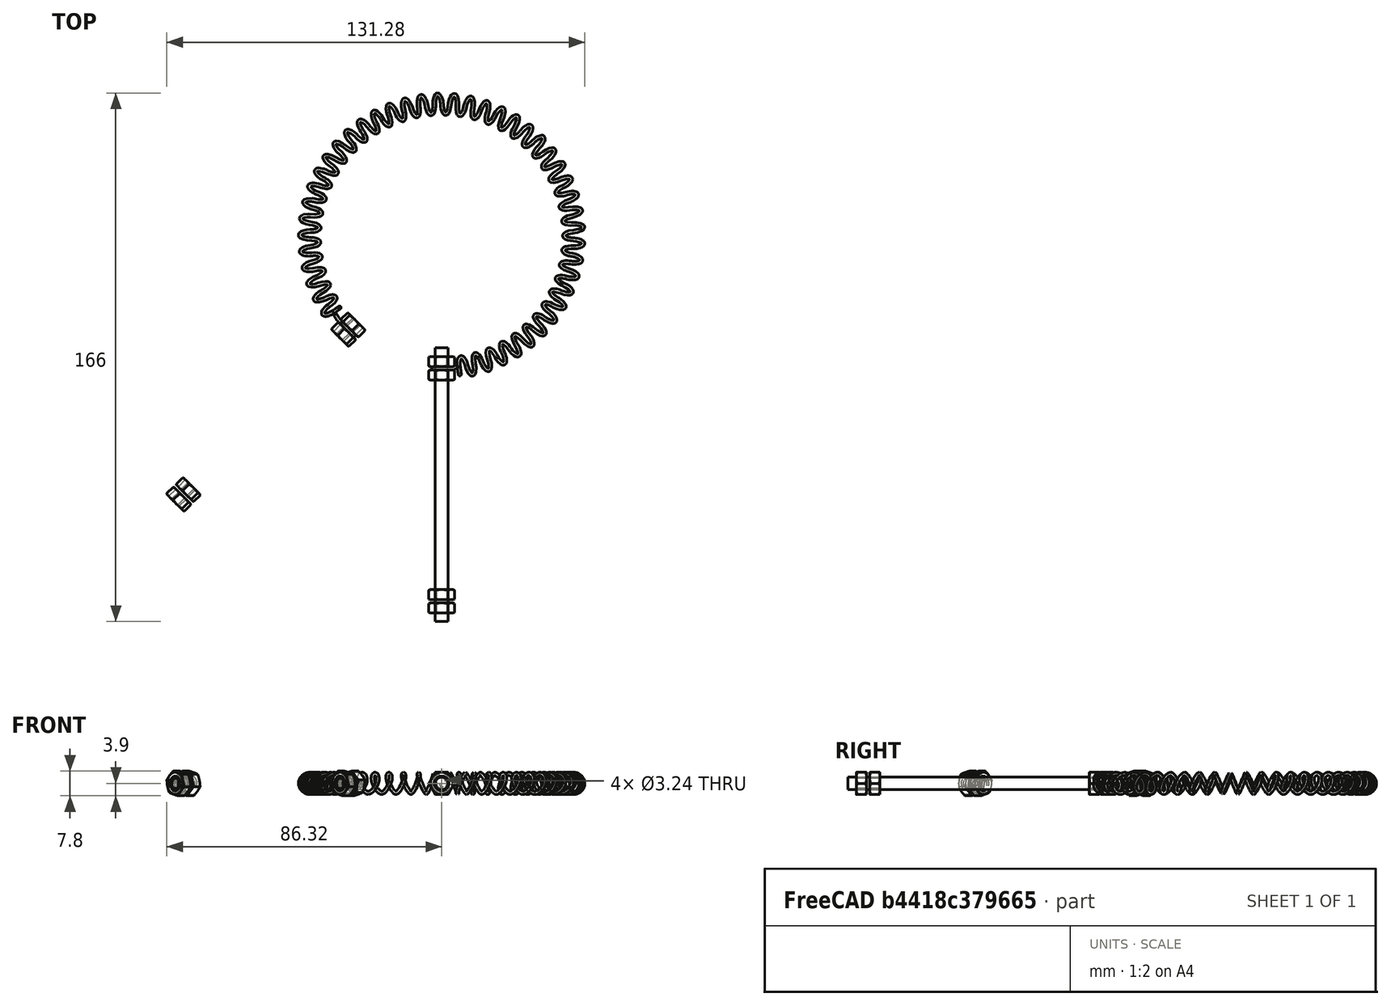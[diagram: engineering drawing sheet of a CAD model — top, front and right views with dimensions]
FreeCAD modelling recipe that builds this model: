
FCSTD DOCUMENT  (FreeCAD 1.0R39319 (Git))
Label: OCT-HELEM-A
License: Creative Commons Attribution 4.0
LicenseURL: https://creativecommons.org/licenses/by/4.0/
objects: Sketcher::SketchObject×9, Part::FeaturePython×9, PartDesign::Plane×3, PartDesign::SubShapeBinder×3, PartDesign::Line×2, PartDesign::Body×2, App::Part×2, App::LinkElement×2, App::VarSet×1, PartDesign::Point×1, PartDesign::AdditivePipe×1, PartDesign::Pad×1, App::Link×1, App::DocumentObjectGroup×1
note: 44 computed .brp shape members not serialized (recipe doc carries the construction recipe); baked Part::Feature solids carry a one-line shape summary decoded from their .brp

FEATURE [App::VarSet] VarSet  label="dims"
  arcAngle = 300
  barLength = 86
  brickThickness = 76
  chamberDiameter = 70
  coilDiameter = 6.02
  dTerminal = 4
  lWire = 866.98
  loopDiameter = 83
  pitch = 4.89634
  wireDiameter = 1.02
  expr: barLength = brickThickness + 10 mm
  expr: pitch = pi * coilDiameter * tan(asin(0.5 * loopDiameter * arcAngle * pi / (180 * lWire * 1 deg)))
FEATURE [Sketcher::SketchObject] Sketch006  label="coil path"
  ArcFitTolerance = 1e-06
  AttachmentSupport = -> [XY_Plane002]
  FullyConstrained = true
  MakeInternals = false
  MapMode = 5
  expr: Constraints[1] = <<dims>>.arcAngle
  expr: Constraints[3] = <<dims>>.loopDiameter / 2
  sketch-geometry (5):
    g0: ArcOfCircle CenterX=0 CenterY=0 CenterZ=0 NormalX=0 NormalY=0 NormalZ=1 AngleXU=0 Radius=41.5 StartAngle=4.84329 EndAngle=10.0793
    g1: LineSegment [constr] StartX=0 StartY=0 StartZ=0 EndX=-15.8814 EndY=-38.341 EndZ=0
    g2: LineSegment [constr] StartX=-32.9242 StartY=-25.2636 StartZ=0 EndX=-15.8814 EndY=-38.341 EndZ=0
    g3: LineSegment [constr] StartX=5.41684 StartY=-41.145 StartZ=0 EndX=-15.8814 EndY=-38.341 EndZ=0
    g4: LineSegment [constr] StartX=0 StartY=0 StartZ=0 EndX=-32.9242 EndY=-25.2636 EndZ=0
  constraints (14):
    c: Coincident(g0,g-1)
    c: Angle(g0) = 5.23599
    c: Coincident(g1,g0)
    c: Radius(g0) = 41.5
    c: PointOnObject(g1,g0)
    c: Coincident(g2,g0)
    c: Coincident(g2,g1)
    c: Coincident(g3,g0)
    c: Coincident(g3,g1)
    c: Equal(g2,g3)
    c: Coincident(g4,g0)
    c: Coincident(g4,g0)
    c: Angle(g-2,g4) = 2.22529
    c: Angle(g-2,g1) = 2.74889
FEATURE [PartDesign::Plane] DatumPlane  label="coil start right"
  AttachmentOffset = pos=(0,0,0) rot=(0,1,0;0.1309rad)
  AttachmentSupport = -> [YZ_Plane003]
  Length = 114.074
  MapMode = 5
  Placement = pos=(0,0,0) rot=(0.527011,0.600941,0.600941;2.17155rad)
  ResizeMode = 0
  Width = 64.1376
  expr: .AttachmentOffset.Rotation.Pitch = -22.5 + (360 - <<dims>>.arcAngle / deg) / 2
FEATURE [Part::FeaturePython] PathHelix  # WARN: FeaturePython — macro-defined, semantics opaque (R4)
  Count = 44.3787
  ExtraHalf = false
  Join = true
  Pitch = 4.89634
  Radius = 3.01
  Resolution = 4
  Reverse = true
  Rotation = 180
  Spine = -> Sketch006
  expr: Pitch = <<dims>>.pitch
  expr: Radius = <<dims>>.coilDiameter / 2
FEATURE [PartDesign::SubShapeBinder] Binder  label="loop binder"
  BindCopyOnChange = 0
  BindMode = 0
  ClaimChildren = false
  Context = -> Part [Part001.Body001.Binder.]
  Fuse = false
  MakeFace = true
  OffsetFill = false
  OffsetIntersection = false
  OffsetJoinType = 0
  OffsetOpenResult = false
  PartialLoad = false
  Relative = true
  Support = -> [Sketch006]
  _Version = 2
FEATURE [Sketcher::SketchObject] Sketch  label="terminal loop right"
  ArcFitTolerance = 1e-06
  AttachmentOffset = pos=(0,0,41.5) rot=(0,0,1;0rad)
  AttachmentSupport = -> [XZ_Plane003]
  FullyConstrained = true
  MakeInternals = false
  MapMode = 5
  Placement = pos=(0,-41.5,9.2e-15) rot=(1,0,0;1.5708rad)
  expr: .AttachmentOffset.Base.z = <<dims>>.loopDiameter / 2
  expr: Constraints[3] = (<<dims>>.dTerminal + <<dims>>.wireDiameter) / 2
  sketch-geometry (2):
    g0: ArcOfCircle CenterX=0 CenterY=0 CenterZ=0 NormalX=0 NormalY=0 NormalZ=1 AngleXU=0 Radius=2.51 StartAngle=0.288902 EndAngle=5.78669
    g1: ArcOfCircle CenterX=3.36454 CenterY=1 CenterZ=0 NormalX=0 NormalY=0 NormalZ=1 AngleXU=0 Radius=1 StartAngle=3.4305 EndAngle=4.71239
  constraints (6):
    c: Coincident(g0,g-1)
    c: Tangent(g0,g1) = 1.5708
    c: Tangent(g1,g-1) = -1.5708
    c: Radius(g0) = 2.51
    c: Radius(g1) = 1
    c: Angle(g0) = 5.49779
FEATURE [Sketcher::SketchObject] Sketch007  label="xy transition right"
  ArcFitTolerance = 1e-06
  AttachmentSupport = -> [XY_Plane003]
  ExternalGeometry = -> [Sketch,Binder]
  FullyConstrained = true
  MakeInternals = false
  MapMode = 5
  sketch-geometry (3):
    g0: ArcOfCircle CenterX=3.36454 CenterY=-40.4973 CenterZ=0 NormalX=0 NormalY=0 NormalZ=1 AngleXU=0 Radius=1.00271 StartAngle=4.71239 EndAngle=5.33537
    g1: ArcOfCircle CenterX=4.53463 CenterY=-42.126 CenterZ=0 NormalX=0 NormalY=0 NormalZ=1 AngleXU=0 Radius=1.00271 StartAngle=0.1309 EndAngle=2.19378
    g2: LineSegment [constr] StartX=5.52876 StartY=-41.9951 StartZ=0 EndX=0 EndY=0 EndZ=0
  constraints (7):
    c: Tangent(g1,g0) = 1.5708
    c: Tangent(g2,g1) = -1.5708
    c: Coincident(g2,g-1)
    c: PointOnObject(g-4,g2)
    c: PointOnObject(g0,g-4)
    c: Tangent(g-3,g0) = -1.5708
    c: Equal(g1,g0)
FEATURE [PartDesign::SubShapeBinder] Binder001  label="coil binder"
  BindCopyOnChange = 0
  BindMode = 0
  ClaimChildren = false
  Context = -> Part [Part001.Body001.Binder001.]
  Fuse = false
  MakeFace = true
  OffsetFill = false
  OffsetIntersection = false
  OffsetJoinType = 0
  OffsetOpenResult = false
  PartialLoad = false
  Relative = true
  Support = -> [PathHelix]
  _Version = 2
FEATURE [Sketcher::SketchObject] Sketch008  label="coil transition right"
  ArcFitTolerance = 1e-06
  AttachmentSupport = -> [DatumPlane]
  ExternalGeometry = -> [Binder001,Sketch007]
  FullyConstrained = true
  MakeInternals = false
  MapMode = 5
  Placement = pos=(0,0,0) rot=(0.527011,0.600941,0.600941;2.17155rad)
  expr: Constraints[1] = <<dims>>.loopDiameter / 2
  expr: Constraints[2] = <<dims>>.coilDiameter
  sketch-geometry (3):
    g0: Circle [constr] CenterX=-41.5 CenterY=0 CenterZ=0 NormalX=0 NormalY=0 NormalZ=1 AngleXU=0 Radius=3.01
    g1: ArcOfCircle CenterX=-42.3575 CenterY=1.38287 CenterZ=0 NormalX=0 NormalY=0 NormalZ=1 AngleXU=0 Radius=1.38287 StartAngle=2.12583 EndAngle=4.71238
    g2: ArcOfCircle CenterX=-41.5 CenterY=0 CenterZ=0 NormalX=0 NormalY=0 NormalZ=1 AngleXU=0 Radius=3.01 StartAngle=1.5708 EndAngle=2.12583
  constraints (8):
    c: PointOnObject(g0,g-1)
    c: DistanceX(g0,g-1) = 41.5
    c: Diameter(g0) = 6.02
    c: Coincident(g1,g-4)
    c: Tangent(g1,g-1)
    c: Coincident(g2,g-3)
    c: Coincident(g2,g0)
    c: Tangent(g1,g2) = -1.5708
FEATURE [Sketcher::SketchObject] Sketch009  label="wire cross section"
  ArcFitTolerance = 1e-06
  AttachmentSupport = -> [YZ_Plane003]
  FullyConstrained = true
  MakeInternals = false
  MapMode = 5
  Placement = pos=(0,0,0) rot=(0.57735,0.57735,0.57735;2.0944rad)
  expr: Constraints[0] = <<dims>>.wireDiameter
  expr: Constraints[1] = <<dims>>.loopDiameter / 2
  expr: Constraints[2] = (<<dims>>.dTerminal + <<dims>>.wireDiameter) / 2
  sketch-geometry (1):
    g0: Circle CenterX=-41.5 CenterY=-2.51 CenterZ=0 NormalX=0 NormalY=0 NormalZ=1 AngleXU=0 Radius=0.51
  constraints (3):
    c: Diameter(g0) = 1.02
    c: DistanceX(g0,g-1) = 41.5
    c: DistanceY(g0,g-1) = 2.51
FEATURE [PartDesign::Line] DatumLine  label="terminal axis left"
  AttacherType = Attacher::AttachEngineLine
  AttachmentOffset = pos=(0,0,0) rot=(0,-1,0;0.785398rad)
  AttachmentSupport = -> [Y_Axis003]
  Length = 20
  MapMode = 29
  Placement = pos=(0,0,0) rot=(0.281085,0.678598,0.678598;2.59356rad)
  ResizeMode = 0
FEATURE [PartDesign::Plane] DatumPlane001  label="terminal left plane"
  AttachmentOffset = pos=(0,0,41.5) rot=(0,0,1;0rad)
  AttachmentSupport = -> [DatumLine]
  Length = 142.427
  MapMode = 7
  Placement = pos=(-29.3449,-29.3449,0) rot=(0.862856,-0.357407,-0.357407;1.71777rad)
  ResizeMode = 0
  Width = 65.9072
  expr: .AttachmentOffset.Base.z = <<dims>>.loopDiameter / 2
FEATURE [Sketcher::SketchObject] Sketch010  label="terminal loop left"
  ArcFitTolerance = 1e-06
  AttachmentSupport = -> [DatumPlane001]
  FullyConstrained = true
  MakeInternals = false
  MapMode = 5
  Placement = pos=(-29.3449,-29.3449,0) rot=(0.862856,-0.357407,-0.357407;1.71777rad)
  expr: Constraints[1] = (<<dims>>.dTerminal + <<dims>>.wireDiameter) / 2
  sketch-geometry (2):
    g0: ArcOfCircle CenterX=0 CenterY=0 CenterZ=0 NormalX=0 NormalY=0 NormalZ=1 AngleXU=0 Radius=2.51 StartAngle=3.63809 EndAngle=9.13588
    g1: ArcOfCircle CenterX=-3.36454 CenterY=1 CenterZ=0 NormalX=0 NormalY=0 NormalZ=1 AngleXU=0 Radius=1 StartAngle=4.71239 EndAngle=5.99428
  constraints (6):
    c: Coincident(g0,g-1)
    c: Radius(g0) = 2.51
    c: Radius(g1) = 1
    c: Tangent(g1,g0) = 1.5708
    c: Tangent(g1,g-1) = -1.5708
    c: Angle(g0) = 5.49779
FEATURE [PartDesign::Point] DatumPoint  label="coil start point left"
  AttacherType = Attacher::AttachEnginePoint
  AttachmentSupport = -> [Binder001]
  MapMode = 37
  Placement = pos=(-34.0198,-23.7677,3.01) rot=(0,0,1;0rad)
FEATURE [PartDesign::Plane] DatumPlane002  label="coil start plane left"
  AttachmentSupport = -> [Binder001,Z_Axis003]
  Length = 140.493
  MapMode = 13
  Placement = pos=(-11.3399,-7.92258,1.33667) rot=(0.913595,0.287528,0.287528;1.66104rad)
  ResizeMode = 0
  Width = 65.7925
FEATURE [Sketcher::SketchObject] Sketch011  label="xy transition left"
  ArcFitTolerance = 1e-06
  AttachmentSupport = -> [XY_Plane003]
  ExternalGeometry = -> [Sketch010,Binder001]
  FullyConstrained = true
  MakeInternals = false
  MapMode = 5
  expr: Constraints[4] = <<dims>>.loopDiameter / 2
  sketch-geometry (4):
    g0: ArcOfCircle CenterX=-24.9661 CenterY=-20.2079 CenterZ=0 NormalX=0 NormalY=0 NormalZ=1 AngleXU=0 Radius=9.55715 StartAngle=3.60279 EndAngle=3.92699
    g1: ArcOfCircle CenterX=-32.6292 CenterY=-24.0161 CenterZ=0 NormalX=0 NormalY=0 NormalZ=1 AngleXU=0 Radius=1 StartAngle=2.18061 EndAngle=3.60279
    g2: LineSegment [constr] StartX=-33.5247 StartY=-24.4611 StartZ=0 EndX=0 EndY=3.6e-15 EndZ=0
    g3: LineSegment [constr] StartX=-34.0198 StartY=-23.7677 StartZ=0 EndX=0 EndY=0 EndZ=0
  constraints (9):
    c: Tangent(g0,g-3) = -1.5708
    c: Tangent(g0,g1) = -1.5708
    c: Coincident(g2,g0)
    c: Coincident(g2,g-1)
    c: Distance(g2,g2) = 41.5
    c: Coincident(g3,g-4)
    c: Coincident(g3,g2)
    c: Tangent(g1,g3) = 1.5708
    c: Radius(g1) = 1
FEATURE [Sketcher::SketchObject] Sketch012  label="coil transition left"
  ArcFitTolerance = 1e-06
  AttachmentSupport = -> [DatumPlane002]
  ExternalGeometry = -> [Sketch011,DatumPoint]
  FullyConstrained = true
  MakeInternals = false
  MapMode = 5
  Placement = pos=(-11.3399,-7.92258,1.33667) rot=(0.913595,0.287528,0.287528;1.66104rad)
  sketch-geometry (3):
    g0: Circle [constr] CenterX=-27.6579 CenterY=-1.33667 CenterZ=0 NormalX=0 NormalY=0 NormalZ=1 AngleXU=0 Radius=3.01001
    g1: ArcOfCircle CenterX=-26.6689 CenterY=0.00586924 CenterZ=0 NormalX=0 NormalY=0 NormalZ=1 AngleXU=0 Radius=1.34254 StartAngle=4.71239 EndAngle=7.21908
    g2: ArcOfCircle CenterX=-27.6579 CenterY=-1.33667 CenterZ=0 NormalX=0 NormalY=0 NormalZ=1 AngleXU=0 Radius=3.01001 StartAngle=0.935895 EndAngle=1.5737
  constraints (6):
    c: Coincident(g0,g-3)
    c: PointOnObject(g1,g0)
    c: Coincident(g2,g0)
    c: Tangent(g2,g1) = -1.5708
    c: Tangent(g1,g-3) = 1.5708
    c: Coincident(g2,g-4)
FEATURE [PartDesign::SubShapeBinder] Binder002  label="full path binder"
  BindCopyOnChange = 0
  BindMode = 0
  ClaimChildren = false
  Context = -> Part [Part001.Body001.Binder002.]
  Fuse = false
  MakeFace = true
  OffsetFill = false
  OffsetIntersection = false
  OffsetJoinType = 0
  OffsetOpenResult = false
  PartialLoad = false
  Refine = true
  Relative = true
  Support = -> [Sketch007,Sketch,Sketch011,Sketch008,Sketch010,Sketch012,Binder001]
  _Version = 2
FEATURE [PartDesign::AdditivePipe] AdditivePipe
  AuxilleryCurvelinear = true
  AuxillerySpineTangent = false
  Binormal = (0,0,0)
  Mode = 0
  Placement = pos=(0,0,0) rot=(1,1,1;2.0944rad)
  Profile = -> Sketch009
  Refine = true
  Spine = -> Binder002
  SpineTangent = false
  Suppressed = false
  Transformation = 0
  Transition = 0
FEATURE [PartDesign::Line] DatumLine001  label="terminal axis right"
  AttacherType = Attacher::AttachEngineLine
  AttachmentSupport = -> [Y_Axis003]
  Length = 20
  MapMode = 29
  Placement = pos=(0,0,0) rot=(0,0.707107,0.707107;3.14159rad)
  ResizeMode = 0
FEATURE [PartDesign::Body] Body001  label="element body"
  AllowCompound = false
  Group = -> [DatumPlane,DatumLine001,DatumPlane001,DatumLine,Binder,Binder001,DatumPoint,DatumPlane002,Sketch,Sketch007,Sketch008,Sketch009,Sketch010,Sketch011,Sketch012,Binder002,AdditivePipe]
  Origin = -> Origin003
  Tip = -> AdditivePipe
FEATURE [App::Part] Part001  label="OCT-HWIRE-AA"
  Group = -> [Sketch006,Body001,PathHelix]
  Origin = -> Origin002
FEATURE [Sketcher::SketchObject] Sketch013
  ArcFitTolerance = 1e-06
  AttachmentOffset = pos=(0,0,35) rot=(0,0,1;0rad)
  AttachmentSupport = -> [XZ_Plane]
  FullyConstrained = true
  MakeInternals = false
  MapMode = 5
  Placement = pos=(0,-35,7.8e-15) rot=(1,0,0;1.5708rad)
  expr: .AttachmentOffset.Base.z = <<dims>>.chamberDiameter / 2
  expr: Constraints[1] = <<dims>>.dTerminal
  sketch-geometry (1):
    g0: Circle CenterX=0 CenterY=0 CenterZ=0 NormalX=0 NormalY=0 NormalZ=1 AngleXU=0 Radius=2
  constraints (2):
    c: Coincident(g0,g-1)
    c: Diameter(g0) = 4
FEATURE [PartDesign::Pad] Pad
  Direction = (0,-1,2e-16)
  Length = 86
  Length2 = 10
  Placement = pos=(0,0,0) rot=(1,0,0;1.5708rad)
  Profile = -> Sketch013
  ReferenceAxis = -> Sketch013 [N_Axis]
  Refine = true
  Suppressed = false
  Type = 0
  expr: Length = <<dims>>.barLength
FEATURE [PartDesign::Body] Body  label="OCT-PWBAR-AA"
  AllowCompound = false
  Group = -> [Sketch013,Pad]
  Origin = -> Origin
  Tip = -> Pad
FEATURE [App::LinkElement] Link_i0
  LinkedObject = -> Body
  _LinkOwner = 2349
FEATURE [App::LinkElement] Link_i1
  LinkPlacement = pos=(0,0,0) rot=(0,0,1;-0.785398rad)
  LinkedObject = -> Body
  Placement = pos=(0,0,0) rot=(0,0,1;-0.785398rad)
  _LinkOwner = 2349
FEATURE [App::Link] Link  label="OCT-PWBAR-AA"
  ElementCount = 2
  ElementList = -> [Link_i0,Link_i1]
  LinkedObject = -> Body
FEATURE [Part::FeaturePython] Nut  label="M4-Nut"  # WARN: FeaturePython — macro-defined, semantics opaque (R4)
  BaseObject = -> Link [Link_i0.Pad.Edge2]
  Diameter = 6
  Invert = true
  LeftHanded = false
  MatchOuter = false
  Offset = -5.99
  OffsetAngle = 0
  Placement = pos=(0,-40.99,9.1e-15) rot=(-1,0,0;1.5708rad)
  Thread = false
  Type = 31
  expr: Offset = (<<dims>>.chamberDiameter - <<dims>>.loopDiameter + <<dims>>.wireDiameter) / 2
FEATURE [Part::FeaturePython] Nut001  label="M4-Nut"  # WARN: FeaturePython — macro-defined, semantics opaque (R4)
  BaseObject = -> Nut [Edge27]
  Diameter = 6
  Invert = true
  LeftHanded = false
  MatchOuter = false
  Offset = 1.02
  OffsetAngle = 0
  Placement = pos=(0,-42.01,9.3e-15) rot=(1,0,0;1.5708rad)
  Thread = false
  Type = 31
  expr: Offset = <<dims>>.wireDiameter
FEATURE [Part::FeaturePython] Nut002  label="M4-Nut"  # WARN: FeaturePython — macro-defined, semantics opaque (R4)
  BaseObject = -> Link [Link_i0.Pad.Edge3]
  Diameter = 6
  Invert = false
  LeftHanded = false
  MatchOuter = true
  Offset = -10
  OffsetAngle = 0
  Placement = pos=(0,-111,2.46e-14) rot=(1,0,0;1.5708rad)
  Thread = false
  Type = 31
  expr: Offset = -(<<dims>>.barLength - <<dims>>.brickThickness)
FEATURE [Part::FeaturePython] Nut003  label="M4-Nut"  # WARN: FeaturePython — macro-defined, semantics opaque (R4)
  BaseObject = -> Nut002 [Edge2]
  Diameter = 6
  Invert = false
  LeftHanded = false
  MatchOuter = true
  Offset = 1
  OffsetAngle = 0
  Placement = pos=(0,-115.2,2.56e-14) rot=(1,0,0;1.5708rad)
  Thread = false
  Type = 31
FEATURE [Part::FeaturePython] Nut004  label="M4-Nut"  # WARN: FeaturePython — macro-defined, semantics opaque (R4)
  BaseObject = -> Link [Link_i1.Pad.Edge2]
  Diameter = 6
  Invert = true
  LeftHanded = false
  MatchOuter = true
  Offset = -5.99
  OffsetAngle = 0
  Placement = pos=(-28.9843,-28.9843,1.55e-14) rot=(-0.707107,0.707107,0;1.5708rad)
  Thread = false
  Type = 31
  expr: Offset = (<<dims>>.chamberDiameter - <<dims>>.loopDiameter + <<dims>>.wireDiameter) / 2
FEATURE [Part::FeaturePython] Nut005  label="M4-Nut"  # WARN: FeaturePython — macro-defined, semantics opaque (R4)
  BaseObject = -> Nut004 [Edge50]
  Diameter = 6
  Invert = true
  LeftHanded = false
  MatchOuter = true
  Offset = 1.02
  OffsetAngle = 0
  Placement = pos=(-29.7056,-29.7056,1.57e-14) rot=(0.707107,-0.707107,0;1.5708rad)
  Thread = false
  Type = 31
  expr: Offset = <<dims>>.wireDiameter
FEATURE [Part::FeaturePython] Nut006  label="M4-Nut"  # WARN: FeaturePython — macro-defined, semantics opaque (R4)
  BaseObject = -> Link [Link_i1.Pad.Edge3]
  Diameter = 6
  Invert = false
  LeftHanded = false
  MatchOuter = true
  Offset = -10
  OffsetAngle = 0
  Placement = pos=(-78.4889,-78.4889,2.62e-14) rot=(0.707107,-0.707107,0;1.5708rad)
  Thread = false
  Type = 31
  expr: Offset = -(<<dims>>.barLength - <<dims>>.brickThickness)
FEATURE [Part::FeaturePython] Nut007  label="M4-Nut"  # WARN: FeaturePython — macro-defined, semantics opaque (R4)
  BaseObject = -> Nut006 [Edge2]
  Diameter = 6
  Invert = false
  LeftHanded = false
  MatchOuter = true
  Offset = 1
  OffsetAngle = 0
  Placement = pos=(-81.4587,-81.4587,2.67e-14) rot=(0.707107,-0.707107,0;1.5708rad)
  Thread = false
  Type = 31
FEATURE [App::DocumentObjectGroup] Group  label="Nuts"
  Group = -> [Nut,Nut001,Nut002,Nut003,Nut004,Nut005,Nut007,Nut006]
FEATURE [App::Part] Part  label="OCT-HELEM-A"
  Group = -> [Part001,Body,Link,Nut001,Nut,Group,Nut002,Nut003,Nut004,Nut005,Nut007,Nut006]
  Origin = -> Origin004
